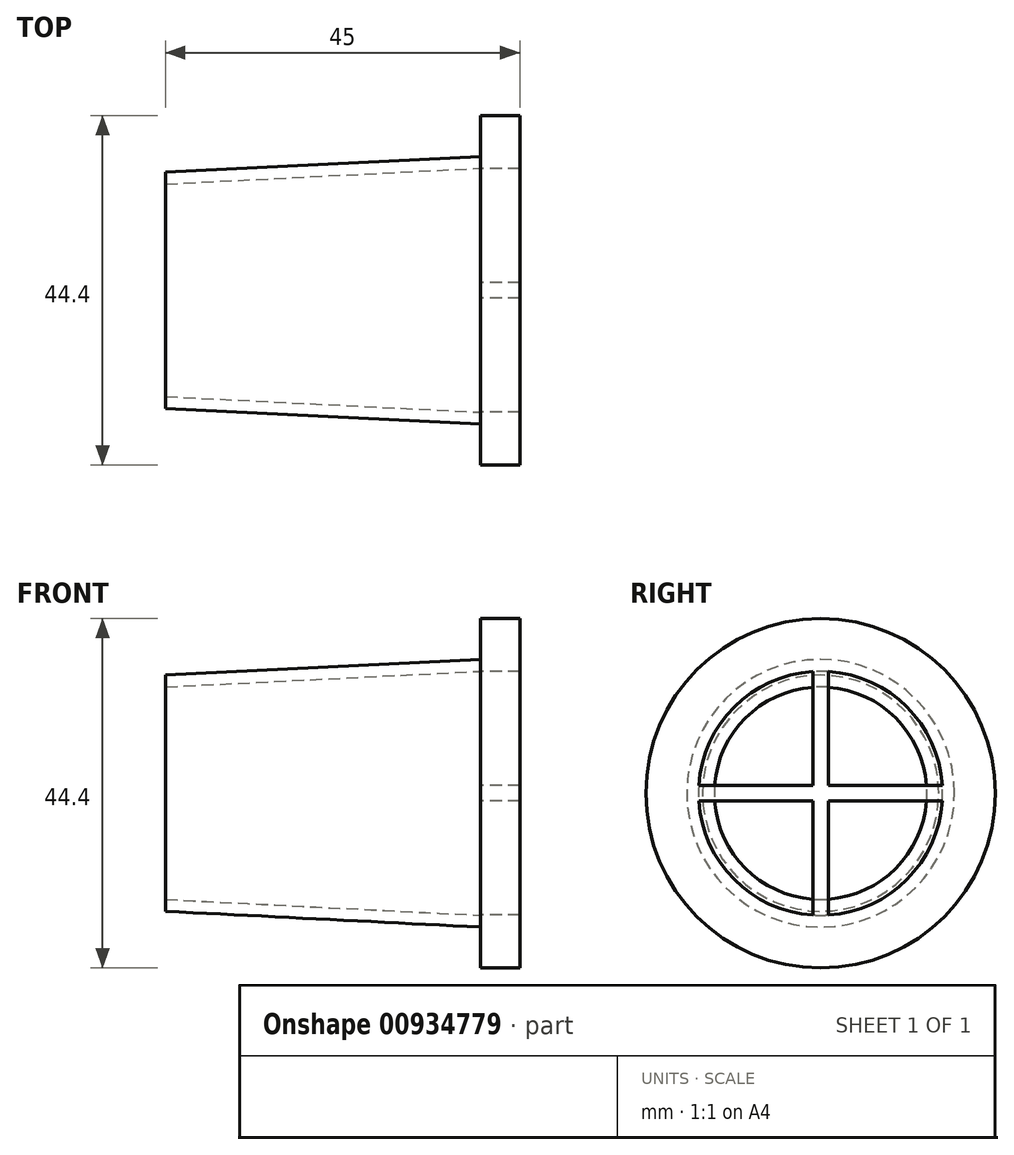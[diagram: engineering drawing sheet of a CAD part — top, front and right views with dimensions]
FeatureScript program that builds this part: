
annotation { "Feature Type Name" : "Feature", "Feature Type Description" : "" }
export const myFeature = defineFeature(function(context is Context, id is Id, definition is map)
    precondition{}
    {
        {
            var Q0;
            Q0=qCreatedBy(makeId("Top.planeOp"),FACE);
            var sketch = newSketch(context, id + "F0", { "sketchPlane" : qUnion([Q0])});
            skLineSegment(sketch, "E0", {"start": v(0, 15.5) * mm, "end": v(-40, 13.5) * mm});
            skLineSegment(sketch, "E1", {"start": v(-40, 13.5) * mm, "end": v(-40, 15) * mm});
            skLineSegment(sketch, "E2", {"start": v(-40, 15) * mm, "end": v(0, 17) * mm});
            skLineSegment(sketch, "E3", {"start": v(0, 17) * mm, "end": v(0, 15.5) * mm});
            skLineSegment(sketch, "E4", {"start": v(0, 0) * mm, "end": v(-42.81, 0) * mm});
            skSolve(sketch);
        }
        {
            var Q0;
            Q0=makeQuery(id+"F0.imprint","IMPRINT",FACE,{"disambiguationData":[TD([[makeQuery(id+"F0.imprint","IMPRINT",EDGE,{"derivedFrom":sQuery(id+"F0.wireOp",EDGE,"E0")}),-1.0]])]});
            var Q1;
            Q1=sQuery(id+"F0.wireOp",EDGE,"E4");
            revolve(context, id + "F1", {"surfaceOperationType" : NewSurfaceOperationType.NEW, "entities" : qUnion([Q0]), "axis" : qUnion([Q1]), "revolveType" : RevolveType.FULL});
        }
        {
            var Q0;
            Q0=makeQuery(id+"F1.opRevolve","SWEPT_FACE",FACE,{"disambiguationData":[OSD([sQuery(id+"F0.wireOp",EDGE,"E3")])]});
            var sketch = newSketch(context, id + "F2", { "sketchPlane" : qUnion([Q0])});
            skCircle(sketch, "E5", {"center": v(0, 0) * mm, "radius": 22.2 * mm});
            skArc(sketch, "E6", {"start": v(15.47, 1) * mm, "mid": v(10.96, 10.96) * mm, "end": v(1, 15.47) * mm});
            skLineSegment(sketch, "E7", {"start": v(1, 15.47) * mm, "end": v(1, 1) * mm});
            skLineSegment(sketch, "E8", {"start": v(15.47, 1) * mm, "end": v(1, 1) * mm});
            skLineSegment(sketch, "E9.MirrorCS", {"start": v(15.47, -1) * mm, "end": v(1, -1) * mm});
            skLineSegment(sketch, "E10.MirrorCS", {"start": v(-1, 15.47) * mm, "end": v(-1, 1) * mm});
            skPoint(sketch, "E11.orphan", {"position": v(16.65, -1) * mm});
            skPoint(sketch, "E12.orphan", {"position": v(16.65, 1) * mm});
            skArc(sketch, "E13.trimOffspring", {"start": v(-1, 15.47) * mm, "mid": v(-10.96, 10.96) * mm, "end": v(-15.47, 1) * mm});
            skPoint(sketch, "E14.orphan", {"position": v(1, 17.8) * mm});
            skPoint(sketch, "E15.orphan", {"position": v(-1, 17.8) * mm});
            skArc(sketch, "E16.trimOffspring", {"start": v(-15.47, -1) * mm, "mid": v(-10.96, -10.96) * mm, "end": v(-1, -15.47) * mm});
            skPoint(sketch, "E17.orphan", {"position": v(-17.54, 1) * mm});
            skPoint(sketch, "E18.orphan", {"position": v(-17.54, -1) * mm});
            skArc(sketch, "E19.trimOffspring", {"start": v(1, -15.47) * mm, "mid": v(10.96, -10.96) * mm, "end": v(15.47, -1) * mm});
            skPoint(sketch, "E20.orphan", {"position": v(1, -16.56) * mm});
            skPoint(sketch, "E21.orphan", {"position": v(-1, -16.56) * mm});
            skLineSegment(sketch, "E22.trimOffspring", {"start": v(-1, -1) * mm, "end": v(-15.47, -1) * mm});
            skLineSegment(sketch, "E23.trimOffspring", {"start": v(1, -1) * mm, "end": v(1, -15.47) * mm});
            skLineSegment(sketch, "E24.trimOffspring", {"start": v(-1, 1) * mm, "end": v(-15.47, 1) * mm});
            skLineSegment(sketch, "E25.trimOffspring", {"start": v(-1, -1) * mm, "end": v(-1, -15.47) * mm});
            skSolve(sketch);
        }
        {
            var Q0;
            {var subQ0=sQuery(id+"F2.wireOp",EDGE,"E7");var subQ16=sQuery(id+"F2.wireOp",EDGE,"E8");var subQ20=makeQuery(id+"F2.imprint","INTERSECT",VERTEX,{"derivedFrom":[subQ0,subQ16]});Q0=makeQuery(id+"F2.imprint","IMPRINT",FACE,{"disambiguationData":[TD([[makeQuery(id+"F2.imprint","IMPRINT",EDGE,{"disambiguationData":[TD([[subQ20,1.0]])],"derivedFrom":subQ0}),-1.0]])]});}
            var Q1;
            {var subQ11=sQuery(id+"F2.wireOp",EDGE,"E6");Q1=makeQuery(id+"F2.imprint","IMPRINT",FACE,{"disambiguationData":[TD([[makeQuery(id+"F2.imprint","IMPRINT",EDGE,{"derivedFrom":subQ11}),-1.0]])]});}
            var Q2;
            Q2=makeQuery(id+"F2.imprint","IMPRINT",FACE,{"disambiguationData":[TD([[makeQuery(id+"F2.imprint","IMPRINT",EDGE,{"derivedFrom":sQuery(id+"F2.wireOp",EDGE,"E5")}),1.0]])]});
            extrude(context, id + "F3", {"entities" : qUnion([Q0, Q1, Q2]), "operationType" : NewBodyOperationType.ADD, "depth" : 5 * mm, "offsetDistance" : 25 * mm});
        }
    });
